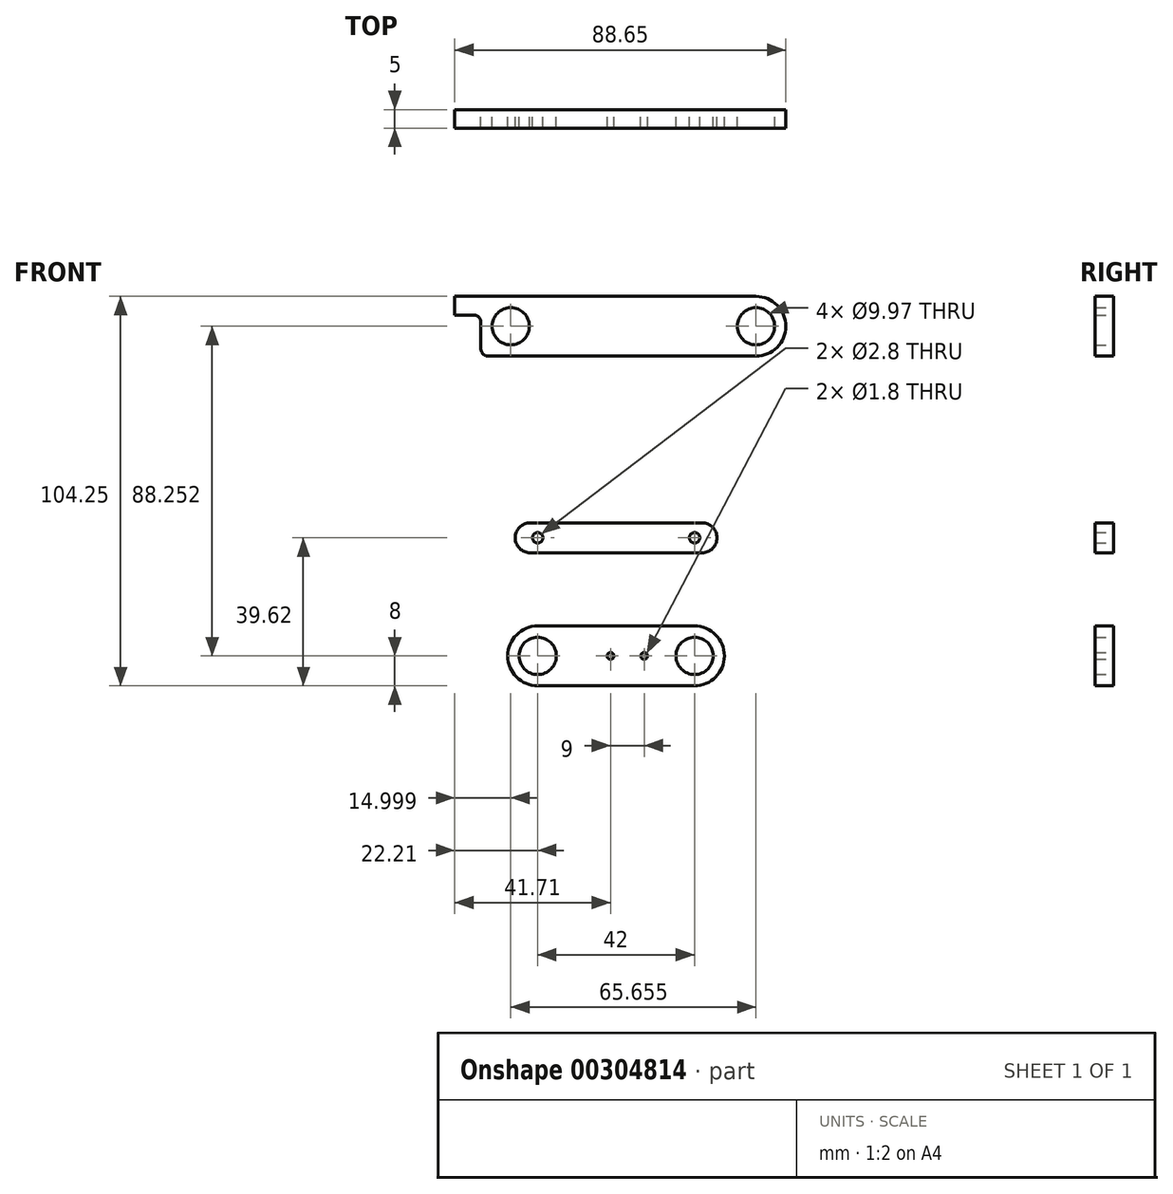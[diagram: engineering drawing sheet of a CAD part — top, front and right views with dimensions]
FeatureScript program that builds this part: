
annotation { "Feature Type Name" : "Feature", "Feature Type Description" : "" }
export const myFeature = defineFeature(function(context is Context, id is Id, definition is map)
    precondition{}
    {
        {
            var Q0;
            Q0=qCreatedBy(makeId("Front.planeOp"),FACE);
            var sketch = newSketch(context, id + "F0", { "sketchPlane" : qUnion([Q0])});
            skPoint(sketch, "E0", {"position": v(-74.78, 0) * mm});
            skPoint(sketch, "E1", {"position": v(0, 0) * mm});
            skPoint(sketch, "E2", {"position": v(8.7, -18.18) * mm});
            skPoint(sketch, "E3", {"position": v(11.78, -63.82) * mm});
            skPoint(sketch, "E4", {"position": v(-71.78, -13) * mm});
            skLineSegment(sketch, "E5", {"start": v(-71.78, -13) * mm, "end": v(8.7, -18.18) * mm});
            skLineSegment(sketch, "E6", {"start": v(-56.81, -13.96) * mm, "end": v(11.78, -63.82) * mm});
            skLineSegment(sketch, "E7.bottom", {"start": v(37.44, 126.92) * mm, "end": v(-34.21, 126.92) * mm});
            skLineSegment(sketch, "E7.top", {"start": v(37.44, 142.92) * mm, "end": v(-32.21, 142.92) * mm});
            skLineSegment(sketch, "E7.left", {"start": v(45.44, 134.92) * mm, "end": v(45.44, 134.92) * mm});
            skPoint(sketch, "E7.middle", {"position": v(0, 134.92) * mm});
            skCircle(sketch, "E8", {"center": v(37.44, 134.92) * mm, "radius": 4.99 * mm});
            skPoint(sketch, "E8.centerSnap0", {"position": v(45.44, 134.92) * mm});
            skLineSegment(sketch, "E9.bottom", {"start": v(23, 74.3) * mm, "end": v(-23, 74.3) * mm});
            skLineSegment(sketch, "E9.top", {"start": v(23, 82.3) * mm, "end": v(-23, 82.3) * mm});
            skLineSegment(sketch, "E9.left", {"start": v(27, 78.3) * mm, "end": v(27, 78.3) * mm});
            skLineSegment(sketch, "E9.right", {"start": v(-27, 78.3) * mm, "end": v(-27, 78.3) * mm});
            skPoint(sketch, "E9.middle", {"position": v(0, 78.3) * mm});
            skLineSegment(sketch, "E10.bottom", {"start": v(21, 38.67) * mm, "end": v(-21, 38.67) * mm});
            skLineSegment(sketch, "E10.top", {"start": v(21, 54.67) * mm, "end": v(-21, 54.67) * mm});
            skLineSegment(sketch, "E10.left", {"start": v(29, 46.67) * mm, "end": v(29, 46.67) * mm});
            skLineSegment(sketch, "E10.right", {"start": v(-29, 46.67) * mm, "end": v(-29, 46.67) * mm});
            skPoint(sketch, "E10.middle", {"position": v(0, 46.67) * mm});
            skCircle(sketch, "E11", {"center": v(-21, 78.3) * mm, "radius": 1.4 * mm});
            skPoint(sketch, "E11.centerSnap0", {"position": v(-27, 78.3) * mm});
            skCircle(sketch, "E12", {"center": v(21, 78.3) * mm, "radius": 1.4 * mm});
            skPoint(sketch, "E12.centerSnap0", {"position": v(27, 78.3) * mm});
            skCircle(sketch, "E13", {"center": v(-21, 46.67) * mm, "radius": 4.99 * mm});
            skPoint(sketch, "E14", {"position": v(21, 46.67) * mm});
            skCircle(sketch, "E15.1.0", {"center": v(7.5, 46.67) * mm, "radius": 0.9 * mm});
            skCircle(sketch, "E15.1.1", {"center": v(-1.5, 46.67) * mm, "radius": 0.9 * mm});
            skCircle(sketch, "E16", {"center": v(-28.21, 134.92) * mm, "radius": 4.99 * mm});
            skLineSegment(sketch, "E17", {"start": v(-43.21, 137.92) * mm, "end": v(-38.21, 137.92) * mm});
            skLineSegment(sketch, "E18", {"start": v(-36.21, 135.92) * mm, "end": v(-36.21, 128.92) * mm});
            skPoint(sketch, "E19.visualSharp", {"position": v(-36.21, 137.92) * mm});
            skArc(sketch, "E19.filletArc", {"start": v(-36.21, 135.92) * mm, "mid": v(-36.8, 137.34) * mm, "end": v(-38.21, 137.92) * mm});
            skCircle(sketch, "E20", {"center": v(21, 46.67) * mm, "radius": 4.99 * mm});
            skPoint(sketch, "E21.visualSharp", {"position": v(45.44, 142.92) * mm});
            skArc(sketch, "E21.filletArc", {"start": v(45.44, 134.92) * mm, "mid": v(43.1, 140.58) * mm, "end": v(37.44, 142.92) * mm});
            skPoint(sketch, "E22.visualSharp", {"position": v(45.44, 126.92) * mm});
            skArc(sketch, "E22.filletArc", {"start": v(37.44, 126.92) * mm, "mid": v(43.1, 129.27) * mm, "end": v(45.44, 134.92) * mm});
            skPoint(sketch, "E23.visualSharp", {"position": v(-36.21, 126.92) * mm});
            skArc(sketch, "E23.filletArc", {"start": v(-36.21, 128.92) * mm, "mid": v(-35.62, 127.5) * mm, "end": v(-34.21, 126.92) * mm});
            skPoint(sketch, "E24.visualSharp", {"position": v(-27, 82.3) * mm});
            skArc(sketch, "E24.filletArc", {"start": v(-23, 82.3) * mm, "mid": v(-25.83, 81.12) * mm, "end": v(-27, 78.3) * mm});
            skPoint(sketch, "E25.visualSharp", {"position": v(-27, 74.3) * mm});
            skArc(sketch, "E25.filletArc", {"start": v(-27, 78.3) * mm, "mid": v(-25.83, 75.46) * mm, "end": v(-23, 74.3) * mm});
            skPoint(sketch, "E26.visualSharp", {"position": v(27, 74.3) * mm});
            skArc(sketch, "E26.filletArc", {"start": v(23, 74.3) * mm, "mid": v(25.83, 75.46) * mm, "end": v(27, 78.3) * mm});
            skPoint(sketch, "E27.visualSharp", {"position": v(27, 82.3) * mm});
            skArc(sketch, "E27.filletArc", {"start": v(27, 78.3) * mm, "mid": v(25.83, 81.12) * mm, "end": v(23, 82.3) * mm});
            skPoint(sketch, "E28.visualSharp", {"position": v(-29, 54.67) * mm});
            skArc(sketch, "E28.filletArc", {"start": v(-21, 54.67) * mm, "mid": v(-26.66, 52.33) * mm, "end": v(-29, 46.67) * mm});
            skPoint(sketch, "E29.visualSharp", {"position": v(-29, 38.67) * mm});
            skArc(sketch, "E29.filletArc", {"start": v(-29, 46.67) * mm, "mid": v(-26.66, 41.01) * mm, "end": v(-21, 38.67) * mm});
            skPoint(sketch, "E30.visualSharp", {"position": v(29, 54.67) * mm});
            skArc(sketch, "E30.filletArc", {"start": v(29, 46.67) * mm, "mid": v(26.66, 52.33) * mm, "end": v(21, 54.67) * mm});
            skPoint(sketch, "E31.visualSharp", {"position": v(29, 38.67) * mm});
            skArc(sketch, "E31.filletArc", {"start": v(21, 38.67) * mm, "mid": v(26.66, 41.01) * mm, "end": v(29, 46.67) * mm});
            skLineSegment(sketch, "E32", {"start": v(-32.21, 142.92) * mm, "end": v(-43.21, 142.92) * mm});
            skLineSegment(sketch, "E33", {"start": v(-43.21, 137.92) * mm, "end": v(-43.21, 142.92) * mm});
            skLineSegment(sketch, "E34", {"start": v(-21, 78.3) * mm, "end": v(21, 78.3) * mm});
            skSolve(sketch);
        }
        {
            var Q0;
            Q0=makeQuery(id+"F0.imprint","IMPRINT",FACE,{"disambiguationData":[TD([[makeQuery(id+"F0.imprint","IMPRINT",EDGE,{"derivedFrom":sQuery(id+"F0.wireOp",EDGE,"E7.bottom")}),-1.0]])]});
            var Q1;
            Q1=makeQuery(id+"F0.imprint","IMPRINT",FACE,{"disambiguationData":[TD([[makeQuery(id+"F0.imprint","IMPRINT",EDGE,{"derivedFrom":sQuery(id+"F0.wireOp",EDGE,"E9.bottom")}),-1.0]])]});
            var Q2;
            Q2=makeQuery(id+"F0.imprint","IMPRINT",FACE,{"disambiguationData":[TD([[makeQuery(id+"F0.imprint","IMPRINT",EDGE,{"derivedFrom":sQuery(id+"F0.wireOp",EDGE,"E10.bottom")}),-1.0]])]});
            extrude(context, id + "F1", {"entities" : qUnion([Q0, Q1, Q2]), "depth" : 5 * mm});
        }
    });
